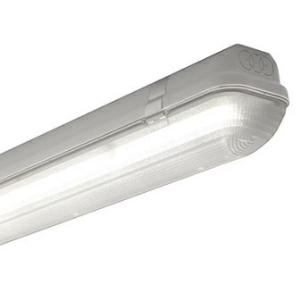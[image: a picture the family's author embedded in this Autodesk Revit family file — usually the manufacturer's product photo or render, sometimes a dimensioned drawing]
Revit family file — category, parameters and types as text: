
# Revit family: 3f_filippi_-_3f_linda_3f_filippi_-_58549_-_3f_linda_led_1x12w_dali_l660
name_source: partatom
category: Lighting Fixtures
units: mm (PartAtom-declared; Revit-internal decimal feet)

## family parameters
Cut with Voids When Loaded = No
Host = Face
Light Source = No
Part Type = Normal
Room Calculation Point = No
Round Connector Dimension = Use Diameter
Shared = No

## types (1)
- 3F Filippi - 3F Linda (1 x LED, 2033 lm, 15 W, 4000 K)
    Apparent Load = 15 VA
    Approval mark = CE
    CIE Flux Codes = 44 77 94 97 100
    Color Rendering = 80
    Color Temperature = 4000 K
    Control Gear = Electronic transformer
    Default Elevation = 1800 mm
    Description = ILLUMINOTECHNICAL
Luminous efficiency 100% (DLOR 97%, ULOR 3%).
Initial luminous flux of the luminaire 2033 lm.
Controlled symmetric distribution.
Installation Interdistance Transv.D = 1.77 x hu - Long.D = 1.17 x hu.
Tabular UGR (CIE 117 - 4H-8H; S=0.25H; 70/50/20): RUG 21.8 - 22.6.
Beam angle: 109° - 64°.
Luminous efficacy 136 lm/W.
Lifetime (L93/B10): 30000 h. (tq+25°C)
Lifetime (L90/B10): 50000 h. (tq+25°C)
Lifetime (L85/B10): 80000 h. (tq+25°C)
Lifetime (L80/B10): 100000 h. (tq+25°C)
Lifetime (L85/B10): 50000 h. (tq+35°C)
Sudden decreased luminous flux after 50000 hours: 0% (C0).
Photobiological safety in compliance with IEC/TR 62778: RG0 risk exempt, (IEC 62471).
In compliance with IEC/EN 62722-2-1 - IEC/EN 62717 standards.

SOURCE
Linear LED module 12W/840.
Energy efficiency class (UE 2019/2020 - UE 2019/2015): D.
CIE 13.3 Colour rendering index: CRI >80 (R9 <50%).
IES TM-30 Fidelity Index: Rf = 84 Rg = 95.
CCT nominal colour temperature 4000 K.
Colour initial tolerance (MacAdam): SDCM 3.

MECHANICAL
Self-extinguishing V2 polycarbonate housing, injection moulded, RAL 7035 grey.
Ecologic anti-aging injected sealing gasket.
Diffuser in self-extinguishing V2 polycarbonate, photo-engraved interior, UV stabilised, injection moulded with smooth outer surface, tamper-proof opening.
Gear-holder reflector in hot-dip galvanised steel, painted with white polyester base.
Snug fit safety snap-lock clips for diffuser mounting in stainless steel, screwdriver opening.
Fixing brackets in stainless steel.
Possibility for technicians to access the interior of the luminaire.
Luminaire with limited surface temperature. - D - (EN 60598-2-24)
Dimensions: 660x100 mm, height 100 mm. Weight 1.08 kg.
IP66 protection degree.
Mechanical strength to impacts IK10 (20 joule).
Glow-wire test resistance 850°C.

ELECTRICAL
Halogen Free DALI-2 DATI (Parts 251, 252, 253), PUSH-DIM, electronic wiring 230V-50/60Hz, power factor 0.85 at full load, THD <25%, constant output current, SELV, class I, 1 driver, 1 DALI addresse.
Power of the luminaire 15 W.
ENEC - CE.
SAFE FLICKER: PstLM=<1 and SVM=<0.4 (IEC TR 61547-1 and IEC TR 63158), to ensure a more comfortable and safe light.
Luminaire compliant with EN 60598-2-22 for power supply from a centralised emergency system CPSS (Central Power Supply System), not incorporated in the luminaire - high risk areas excluded. The default power and flux are 100% in AC and 15% in DC.
Ambient temperature from -20°C to +35°C.
Temperature class T6 max 85°C.
Relative humidity UR: <85%.

INSTALLATION
Ceiling / Suspended / Wall.
All accessories dedicated to this product are available on the Catalog and on our website www.3F-Filippi.com.

APPLICATIONS
Suitable product for food production plants (HACCP), IFS (Food Version 6), BRC (GSFS Food Version 7).
Dry, dusty indoor environments, subject to occasional water splashes.
Virtually shatterproof polycarbonate compatibly with the fumes / atmospheres that compromise the elasticity of plastic materials.
Not suitable for installation on surfaces subject to important vibrations, exposed to weather conditions, on ropes or poles.
Suitable for illumination of public car parks and parking grounds referred to DIN 67528:2018-04.

LIGHT MANAGEMENT
Recommended minimum setting: 10%.
The luminaire, equipped with (DALI-2 DATI) driver, can be controlled manually with 3F Easy Dim technology or automatically/manually with wired or wireless DALI/D2D control systems.
The D2D driver guarantees interoperability with other devices with the same certification by making the following information available:
Device Data (Part 251), Energy Report (Part 252), Diagnosis & Maintenance (Part 253).
In electrical systems without a regulation system (manual or automatic) and DALI bus, a suitable jumper must be made on the DA-DA terminals of the appliance.

WARNING
Fixture not suitable for cold stores with an ambient temperature <0°C and/or relative humidity >85%.
Luminaire designed for disposal/recycling at end-of-life.
Replaceable (LED only) light source by a professional. Replaceable control gear by a professional.
    Height = 100 mm  [stored 0.328084 ft]
    Lamp = 1 x LED
    Lamp Light Flux = 2033 lm
    Lamp Power = 15 W
    Lamp count = 1
    Length = 660 mm
    Lifetime = 50000 h
    Luminous efficacy = 136 lm/W
    Manufacturer = 3F Filippi
    ModVariant = No
    Model = 3F Filippi - 58549 - 3F Linda LED 1x12W DALI L660
    Mounting Place = Ceiling
    Mounting Type = Pendant
    Number of Poles = 1
    OnlyDefault = Yes
    Power Factor = 1
    Product Name = 3F Filippi - 3F Linda
    Product group = pendant luminaire
    ProductGroupID = 9
    Protection Class = Protection class I
    Protection Degree = IP 66
    RLX_Detail_Level = 1
    RLX_Emergency_Light_Flux = 0 lm
    RLX_Emergency_Type = 0
    RLX_Emergency_Type_DB = No
    RlxData = <blob elided: 71061 chars, md5=32d62f2e>
    Socket = socket
    Standby Power = 0 W
    System Light Flux = 2033 lm
    System Power = 15 W
    Type Comments = Product without accessories
    Type Image = 3ffilippi_3f_linda_led_1x.jpg
    URL = http://relux.com
    VarID = ---
    Voltage = 0 V
    Weight = 0.00 kg
    Width = 100 mm  [stored 0.328084 ft]

note: [stored X ft] marks values corroborated as IEEE doubles in the binary element streams (Revit-internal decimal feet)

## geometry (parser evidence)
native form markers: Blend x4, Sweep x9
no freeform markers — native parametric forms only
